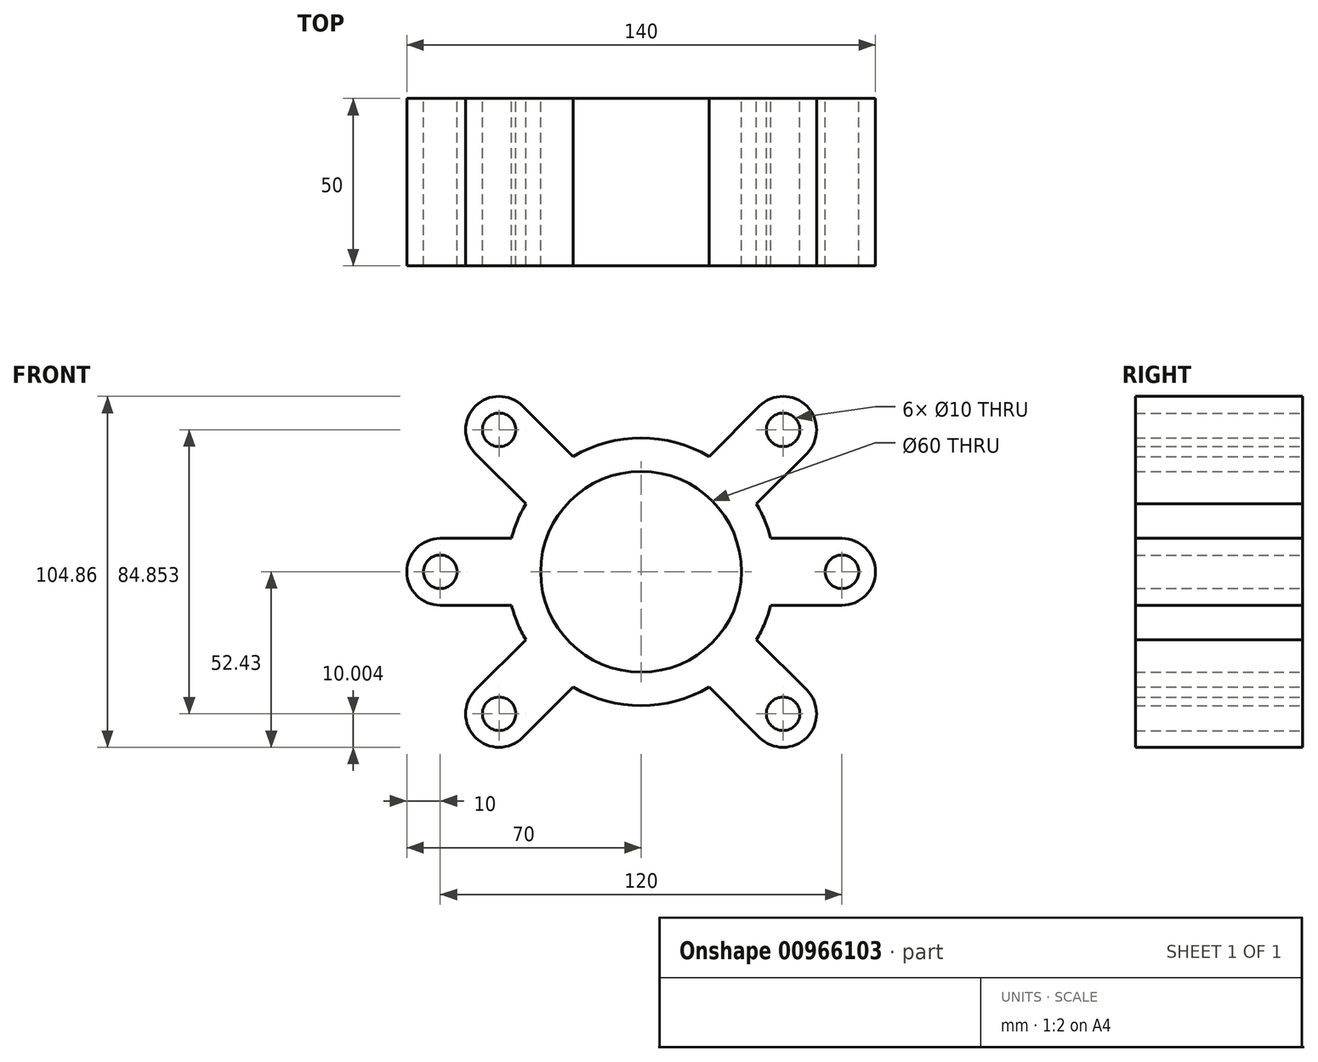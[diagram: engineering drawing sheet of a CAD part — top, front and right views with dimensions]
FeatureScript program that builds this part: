
annotation { "Feature Type Name" : "Feature", "Feature Type Description" : "" }
export const myFeature = defineFeature(function(context is Context, id is Id, definition is map)
    precondition{}
    {
        {
            var Q0;
            Q0=qCreatedBy(makeId("Front.planeOp"),FACE);
            var sketch = newSketch(context, id + "F0", { "sketchPlane" : qUnion([Q0])});
            skArc(sketch, "E0", {"start": v(-38.73, -10) * mm, "mid": v(-36.96, -15.3) * mm, "end": v(-34.46, -20.32) * mm});
            skCircle(sketch, "E1", {"center": v(0, 0) * mm, "radius": 30 * mm});
            skCircle(sketch, "E2", {"center": v(0, 0) * mm, "radius": 60 * mm, "construction": true});
            skCircle(sketch, "E3", {"center": v(-60, 0) * mm, "radius": 5 * mm});
            skArc(sketch, "E4", {"start": v(-59.17, 9.97) * mm, "mid": v(-70, 0) * mm, "end": v(-59.17, -9.97) * mm});
            skLineSegment(sketch, "E5", {"start": v(-60, 10) * mm, "end": v(-38.73, 10) * mm});
            skLineSegment(sketch, "E6.MirrorCS", {"start": v(-60, -10) * mm, "end": v(-38.73, -10) * mm});
            skArc(sketch, "E7.1.0", {"start": v(-48.88, -34.8) * mm, "mid": v(-49.5, -49.5) * mm, "end": v(-34.8, -48.88) * mm});
            skLineSegment(sketch, "E7.1.1", {"start": v(-35.36, -49.5) * mm, "end": v(-20.32, -34.46) * mm});
            skCircle(sketch, "E7.1.2", {"center": v(-42.43, -42.43) * mm, "radius": 5 * mm});
            skLineSegment(sketch, "E7.1.3", {"start": v(-49.5, -35.36) * mm, "end": v(-34.46, -20.32) * mm});
            skArc(sketch, "E7.3.0", {"start": v(34.8, -48.88) * mm, "mid": v(49.5, -49.5) * mm, "end": v(48.88, -34.8) * mm});
            skLineSegment(sketch, "E7.3.1", {"start": v(49.5, -35.36) * mm, "end": v(34.46, -20.32) * mm});
            skCircle(sketch, "E7.3.2", {"center": v(42.43, -42.43) * mm, "radius": 5 * mm});
            skLineSegment(sketch, "E7.3.3", {"start": v(35.36, -49.5) * mm, "end": v(20.32, -34.46) * mm});
            skArc(sketch, "E7.4.0", {"start": v(59.17, -9.97) * mm, "mid": v(70, 0) * mm, "end": v(59.17, 9.97) * mm});
            skLineSegment(sketch, "E7.4.1", {"start": v(60, 10) * mm, "end": v(38.73, 10) * mm});
            skCircle(sketch, "E7.4.2", {"center": v(60, 0) * mm, "radius": 5 * mm});
            skLineSegment(sketch, "E7.4.3", {"start": v(60, -10) * mm, "end": v(38.73, -10) * mm});
            skArc(sketch, "E7.5.0", {"start": v(48.88, 34.8) * mm, "mid": v(49.5, 49.5) * mm, "end": v(34.8, 48.88) * mm});
            skLineSegment(sketch, "E7.5.1", {"start": v(35.36, 49.5) * mm, "end": v(20.32, 34.46) * mm});
            skCircle(sketch, "E7.5.2", {"center": v(42.43, 42.43) * mm, "radius": 5 * mm});
            skLineSegment(sketch, "E7.5.3", {"start": v(49.5, 35.36) * mm, "end": v(34.46, 20.32) * mm});
            skArc(sketch, "E8.trimOffspring", {"start": v(-34.46, 20.32) * mm, "mid": v(-36.96, 15.3) * mm, "end": v(-38.73, 10) * mm});
            skArc(sketch, "E9.trimOffspring", {"start": v(38.73, 10) * mm, "mid": v(15.3, 36.96) * mm, "end": v(-20.32, 34.46) * mm});
            skArc(sketch, "E10.trimOffspring", {"start": v(34.46, -20.32) * mm, "mid": v(36.96, -15.3) * mm, "end": v(38.73, -10) * mm});
            skArc(sketch, "E11.trimOffspring", {"start": v(10, -38.73) * mm, "mid": v(15.3, -36.96) * mm, "end": v(20.32, -34.46) * mm});
            skArc(sketch, "E12.trimOffspring", {"start": v(-20.32, -34.46) * mm, "mid": v(-5.58, -39.6) * mm, "end": v(10, -38.73) * mm});
            skLineSegment(sketch, "E13.4.7.0", {"start": v(-49.5, 35.36) * mm, "end": v(-34.46, 20.32) * mm});
            skArc(sketch, "E13.5.7.0", {"start": v(-34.8, 48.88) * mm, "mid": v(-49.5, 49.5) * mm, "end": v(-48.88, 34.8) * mm});
            skCircle(sketch, "E13.7.7.0", {"center": v(-42.43, 42.43) * mm, "radius": 5 * mm});
            skLineSegment(sketch, "E13.9.7.0", {"start": v(-35.36, 49.5) * mm, "end": v(-20.32, 34.46) * mm});
            skSolve(sketch);
        }
        {
            var Q0;
            Q0 = qSketchRegion(id + "F0", true);
            extrude(context, id + "F1", {"entities" : qUnion([Q0]), "endBound" : BoundingType.SYMMETRIC, "depth" : 50 * mm, "offsetDistance" : 25 * mm});
        }
    });
